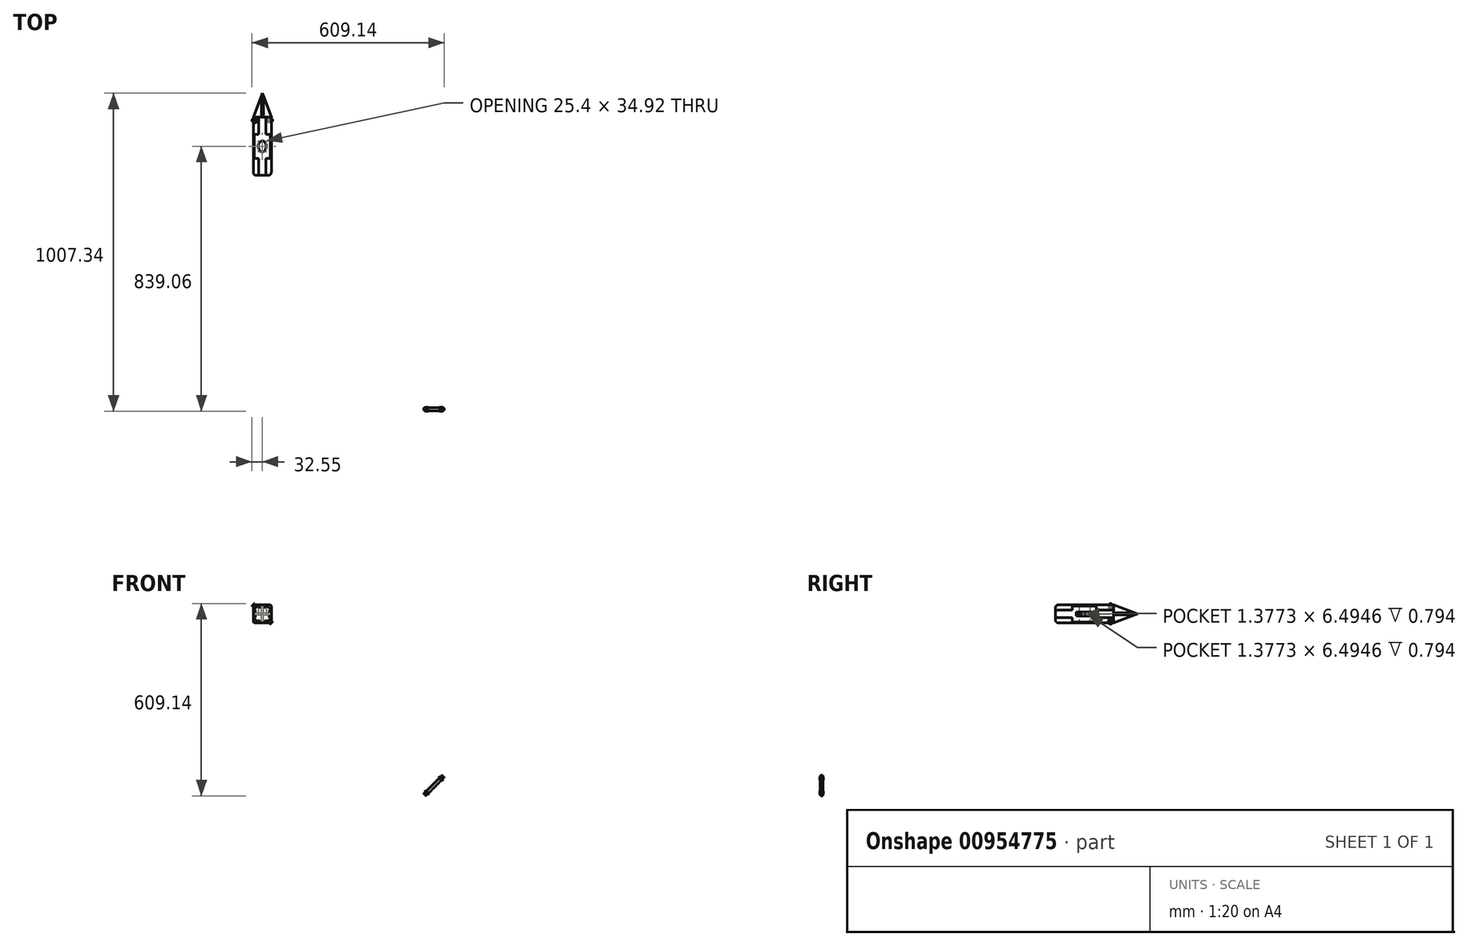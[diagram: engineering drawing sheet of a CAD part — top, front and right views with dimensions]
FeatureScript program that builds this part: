
annotation { "Feature Type Name" : "Feature", "Feature Type Description" : "" }
export const myFeature = defineFeature(function(context is Context, id is Id, definition is map)
    precondition{}
    {
        {
            var Q0;
            Q0=qCreatedBy(makeId("Top.planeOp"),FACE);
            var sketch = newSketch(context, id + "F0", { "sketchPlane" : qUnion([Q0])});
            skEllipse(sketch, "E0", {"center": v(0, 0) * mm, "majorRadius": 12.7 * mm, "minorRadius": 17.46 * mm, "majorAxis": v(1, 0)});
            skSolve(sketch);
        }
        {
            var Q0;
            Q0=qSketchRegion(id+"F0",true);
            extrude(context, id + "F1", {"entities" : qUnion([Q0]), "depth" : 1219.2 * mm, "offsetDistance" : 25.4 * mm});
        }
        {
            var Q0;
            Q0=qCreatedBy(makeId("Front.planeOp"),FACE);
            var sketch = newSketch(context, id + "F2", { "sketchPlane" : qUnion([Q0])});
            skCircle(sketch, "E1.cCircle", {"center": v(0, 1177.87) * mm, "radius": 30.93 * mm, "construction": true});
            skLineSegment(sketch, "E1.0", {"start": v(28.57, 1189.7) * mm, "end": v(28.57, 1166.03) * mm});
            skLineSegment(sketch, "E1.1", {"start": v(28.57, 1166.03) * mm, "end": v(11.84, 1149.3) * mm});
            skLineSegment(sketch, "E1.2", {"start": v(11.84, 1149.3) * mm, "end": v(-11.84, 1149.3) * mm});
            skLineSegment(sketch, "E1.3", {"start": v(-11.84, 1149.3) * mm, "end": v(-28.58, 1166.03) * mm});
            skLineSegment(sketch, "E1.4", {"start": v(-28.58, 1166.03) * mm, "end": v(-28.58, 1189.7) * mm});
            skLineSegment(sketch, "E1.5", {"start": v(-28.57, 1189.7) * mm, "end": v(-11.84, 1206.44) * mm});
            skLineSegment(sketch, "E1.6", {"start": v(-11.84, 1206.44) * mm, "end": v(11.84, 1206.44) * mm});
            skLineSegment(sketch, "E1.7", {"start": v(11.84, 1206.44) * mm, "end": v(28.57, 1189.7) * mm});
            skLineSegment(sketch, "E2.bottom", {"start": v(28.57, 1206.44) * mm, "end": v(-28.58, 1206.44) * mm});
            skLineSegment(sketch, "E2.top", {"start": v(28.57, 1149.3) * mm, "end": v(-28.58, 1149.3) * mm});
            skLineSegment(sketch, "E2.left", {"start": v(28.57, 1206.44) * mm, "end": v(28.57, 1149.3) * mm});
            skLineSegment(sketch, "E2.right", {"start": v(-28.58, 1206.44) * mm, "end": v(-28.58, 1149.3) * mm});
            skSolve(sketch);
        }
        {
            var Q0;
            {var subQ0=sQuery(id+"F2.wireOp",EDGE,"E1.5");Q0=makeQuery(id+"F2.imprint","IMPRINT",FACE,{"disambiguationData":[TD([[makeQuery(id+"F2.imprint","IMPRINT",EDGE,{"derivedFrom":subQ0}),1.0]])]});}
            var Q1;
            {var subQ0=sQuery(id+"F2.wireOp",EDGE,"E1.7");Q1=makeQuery(id+"F2.imprint","IMPRINT",FACE,{"disambiguationData":[TD([[makeQuery(id+"F2.imprint","IMPRINT",EDGE,{"derivedFrom":subQ0}),1.0]])]});}
            var Q2;
            {var subQ4=sQuery(id+"F2.wireOp",EDGE,"E1.1");Q2=makeQuery(id+"F2.imprint","IMPRINT",FACE,{"disambiguationData":[TD([[makeQuery(id+"F2.imprint","IMPRINT",EDGE,{"derivedFrom":subQ4}),-1.0]])]});}
            var Q3;
            {var subQ0=sQuery(id+"F2.wireOp",EDGE,"E1.3");Q3=makeQuery(id+"F2.imprint","IMPRINT",FACE,{"disambiguationData":[TD([[makeQuery(id+"F2.imprint","IMPRINT",EDGE,{"derivedFrom":subQ0}),1.0]])]});}
            var Q4;
            {var subQ0=sQuery(id+"F2.wireOp",EDGE,"E1.1");Q4=makeQuery(id+"F2.imprint","IMPRINT",FACE,{"disambiguationData":[TD([[makeQuery(id+"F2.imprint","IMPRINT",EDGE,{"derivedFrom":subQ0}),1.0]])]});}
            extrude(context, id + "F3", {"entities" : qUnion([Q0, Q1, Q2, Q3, Q4]), "depth" : 38.1 * mm, "offsetDistance" : 25.4 * mm, "hasSecondDirection" : true, "secondDirectionOppositeDirection" : true, "secondDirectionDepth" : 38.1 * mm});
        }
        {
            var Q0;
            {var subQ4=sQuery(id+"F2.wireOp",EDGE,"E1.1");Q0=makeQuery(id+"F2.imprint","IMPRINT",FACE,{"disambiguationData":[TD([[makeQuery(id+"F2.imprint","IMPRINT",EDGE,{"derivedFrom":subQ4}),-1.0]])]});}
            extrude(context, id + "F4", {"entities" : qUnion([Q0]), "operationType" : NewBodyOperationType.ADD, "depth" : 92.07 * mm, "offsetDistance" : 25.4 * mm, "hasSecondDirection" : true, "secondDirectionOppositeDirection" : true, "secondDirectionDepth" : 92.07 * mm});
        }
        {
            var Q0;
            Q0=makeQuery(id+"F4.opExtrude","CAP_FACE",FACE,{"disambiguationData":[OSD([sQuery(id+"F2.wireOp",EDGE,"E1.1"),sQuery(id+"F2.wireOp",EDGE,"E1.3"),sQuery(id+"F2.wireOp",EDGE,"E1.5"),sQuery(id+"F2.wireOp",EDGE,"E1.7"),sQuery(id+"F2.wireOp",EDGE,"E2.bottom"),sQuery(id+"F2.wireOp",EDGE,"E2.top"),sQuery(id+"F2.wireOp",EDGE,"E2.left"),sQuery(id+"F2.wireOp",EDGE,"E2.right")])],"isStart":false});
            fillet(context, id + "F5", {"entities" : qUnion([Q0]), "radius" : 9.52 * mm, "tangentPropagation" : true, "allowEdgeOverflow" : false});
        }
        {
            var Q0;
            Q0=makeQuery(id+"F3.opExtrude","SWEPT_EDGE",EDGE,{"disambiguationData":[OSD([sQuery(id+"F2.wireOp",EDGE,"E2.bottom"),sQuery(id+"F2.wireOp",EDGE,"E2.left")])]});
            var Q1;
            Q1=makeQuery(id+"F3.opExtrude","SWEPT_EDGE",EDGE,{"disambiguationData":[OSD([sQuery(id+"F2.wireOp",EDGE,"E2.top"),sQuery(id+"F2.wireOp",EDGE,"E2.left")])]});
            var Q2;
            Q2=makeQuery(id+"F3.opExtrude","SWEPT_EDGE",EDGE,{"disambiguationData":[OSD([sQuery(id+"F2.wireOp",EDGE,"E2.bottom"),sQuery(id+"F2.wireOp",EDGE,"E2.right")])]});
            var Q3;
            Q3=makeQuery(id+"F3.opExtrude","SWEPT_EDGE",EDGE,{"disambiguationData":[OSD([sQuery(id+"F2.wireOp",EDGE,"E2.top"),sQuery(id+"F2.wireOp",EDGE,"E2.right")])]});
            chamfer(context, id + "F6", {"entities" : qUnion([Q0, Q1, Q2, Q3]), "width" : 3.17 * mm, "tangentPropagation" : true});
        }
        {
            var Q0;
            Q0=qSketchRegion(id+"F0",true);
            extrude(context, id + "F7", {"entities" : qUnion([Q0]), "operationType" : NewBodyOperationType.REMOVE, "depth" : 1219.2 * mm, "offsetDistance" : 25.4 * mm});
        }
        {
            var Q0;
            {var subQ0=sQuery(id+"F2.wireOp",EDGE,"E2.left");Q0=makeQuery(id+"F4.boolean.opBoolean","MERGE",FACE,{"derivedFrom":[makeQuery(id+"F3.opExtrude","SWEPT_FACE",FACE,{"disambiguationData":[OSD([subQ0])]}),makeQuery(id+"F4.opExtrude","SWEPT_FACE",FACE,{"disambiguationData":[OSD([subQ0])]})]});}
            var sketch = newSketch(context, id + "F8", { "sketchPlane" : qUnion([Q0])});
            skLineSegment(sketch, "E3.bottom", {"start": v(28.57, 1162) * mm, "end": v(-28.58, 1162) * mm, "construction": true});
            skLineSegment(sketch, "E3.top", {"start": v(28.57, 1193.74) * mm, "end": v(-28.58, 1193.74) * mm, "construction": true});
            skLineSegment(sketch, "E3.left", {"start": v(28.57, 1162) * mm, "end": v(28.57, 1193.74) * mm, "construction": true});
            skLineSegment(sketch, "E3.right", {"start": v(-28.57, 1162) * mm, "end": v(-28.57, 1193.74) * mm, "construction": true});
            skPoint(sketch, "E3.middle", {"position": v(0, 1177.87) * mm});
            skLineSegment(sketch, "E4", {"start": v(0, 1193.74) * mm, "end": v(-28.58, 1177.87) * mm, "construction": true});
            skLineSegment(sketch, "E5", {"start": v(-28.57, 1177.87) * mm, "end": v(0, 1162) * mm, "construction": true});
            skLineSegment(sketch, "E6", {"start": v(0, 1162) * mm, "end": v(28.58, 1177.87) * mm, "construction": true});
            skLineSegment(sketch, "E7", {"start": v(28.58, 1177.87) * mm, "end": v(0, 1193.74) * mm, "construction": true});
            skLineSegment(sketch, "E8.bottom", {"start": v(24.29, 1173.01) * mm, "end": v(-24.29, 1173.01) * mm});
            skLineSegment(sketch, "E8.top", {"start": v(24.29, 1182.72) * mm, "end": v(-24.29, 1182.72) * mm});
            skLineSegment(sketch, "E8.left", {"start": v(24.29, 1173.01) * mm, "end": v(24.29, 1182.72) * mm});
            skLineSegment(sketch, "E8.right", {"start": v(-24.29, 1173.01) * mm, "end": v(-24.29, 1182.72) * mm});
            skLineSegment(sketch, "E9.bottom", {"start": v(25.87, 1171.43) * mm, "end": v(-25.87, 1171.43) * mm});
            skLineSegment(sketch, "E9.top", {"start": v(25.87, 1184.3) * mm, "end": v(-25.87, 1184.3) * mm});
            skLineSegment(sketch, "E9.left", {"start": v(25.87, 1171.43) * mm, "end": v(25.87, 1184.3) * mm});
            skLineSegment(sketch, "E9.right", {"start": v(-25.87, 1171.43) * mm, "end": v(-25.87, 1184.3) * mm});
            skPoint(sketch, "E10.sketch_text.left.end.orphan", {"position": v(-22.7, 1181.13) * mm});
            skPoint(sketch, "E11", {"position": v(22.7, 1181.13) * mm});
            skPoint(sketch, "E12", {"position": v(22.7, 1174.6) * mm});
            skPoint(sketch, "E13", {"position": v(-22.7, 1174.6) * mm});
            skText(sketch, "E14", { "text": "ARTILLIER", "fontName": "OpenSans-Bold.ttf"});
            const initialGuessF8  = {"E14": [-0.02283, 1.1746, 1, 0, 0.00655]};
            skSetInitialGuess(sketch, initialGuessF8);
            skSolve(sketch);
        }
        {
            var Q0;
            Q0=makeQuery(id+"F8.imprint","IMPRINT",FACE,{"disambiguationData":[TD([[makeQuery(id+"F8.imprint","IMPRINT",EDGE,{"derivedFrom":sQuery(id+"F8.wireOp",EDGE,"E14.sketch_text.stroke-0")}),-1.0]])]});
            var Q1;
            Q1=makeQuery(id+"F8.imprint","IMPRINT",FACE,{"disambiguationData":[TD([[makeQuery(id+"F8.imprint","IMPRINT",EDGE,{"derivedFrom":sQuery(id+"F8.wireOp",EDGE,"E14.sketch_text.stroke-12")}),-1.0]])]});
            var Q2;
            Q2=makeQuery(id+"F8.imprint","IMPRINT",FACE,{"disambiguationData":[TD([[makeQuery(id+"F8.imprint","IMPRINT",EDGE,{"derivedFrom":sQuery(id+"F8.wireOp",EDGE,"E14.sketch_text.stroke-31")}),-1.0]])]});
            var Q3;
            Q3=makeQuery(id+"F8.imprint","IMPRINT",FACE,{"disambiguationData":[TD([[makeQuery(id+"F8.imprint","IMPRINT",EDGE,{"derivedFrom":sQuery(id+"F8.wireOp",EDGE,"E14.sketch_text.stroke-39")}),-1.0]])]});
            var Q4;
            Q4=makeQuery(id+"F8.imprint","IMPRINT",FACE,{"disambiguationData":[TD([[makeQuery(id+"F8.imprint","IMPRINT",EDGE,{"derivedFrom":sQuery(id+"F8.wireOp",EDGE,"E14.sketch_text.stroke-43")}),-1.0]])]});
            var Q5;
            Q5=makeQuery(id+"F8.imprint","IMPRINT",FACE,{"disambiguationData":[TD([[makeQuery(id+"F8.imprint","IMPRINT",EDGE,{"derivedFrom":sQuery(id+"F8.wireOp",EDGE,"E8.bottom")}),1.0]])]});
            var Q6;
            Q6=makeQuery(id+"F8.imprint","IMPRINT",FACE,{"disambiguationData":[TD([[makeQuery(id+"F8.imprint","IMPRINT",EDGE,{"derivedFrom":sQuery(id+"F8.wireOp",EDGE,"E14.sketch_text.stroke-49")}),-1.0]])]});
            var Q7;
            Q7=makeQuery(id+"F8.imprint","IMPRINT",FACE,{"disambiguationData":[TD([[makeQuery(id+"F8.imprint","IMPRINT",EDGE,{"derivedFrom":sQuery(id+"F8.wireOp",EDGE,"E14.sketch_text.stroke-55")}),-1.0]])]});
            var Q8;
            Q8=makeQuery(id+"F8.imprint","IMPRINT",FACE,{"disambiguationData":[TD([[makeQuery(id+"F8.imprint","IMPRINT",EDGE,{"derivedFrom":sQuery(id+"F8.wireOp",EDGE,"E14.sketch_text.stroke-59")}),-1.0]])]});
            var Q9;
            Q9=makeQuery(id+"F8.imprint","IMPRINT",FACE,{"disambiguationData":[TD([[makeQuery(id+"F8.imprint","IMPRINT",EDGE,{"derivedFrom":sQuery(id+"F8.wireOp",EDGE,"E14.sketch_text.stroke-71")}),-1.0]])]});
            extrude(context, id + "F9", {"entities" : qUnion([Q0, Q1, Q2, Q3, Q4, Q5, Q6, Q7, Q8, Q9]), "operationType" : NewBodyOperationType.REMOVE, "oppositeDirection" : true, "depth" : 0.8 * mm, "offsetDistance" : 25.4 * mm});
        }
        {
            var Q0;
            {var subQ0=sQuery(id+"F2.wireOp",EDGE,"E2.right");Q0=makeQuery(id+"F4.boolean.opBoolean","MERGE",FACE,{"derivedFrom":[makeQuery(id+"F3.opExtrude","SWEPT_FACE",FACE,{"disambiguationData":[OSD([subQ0])]}),makeQuery(id+"F4.opExtrude","SWEPT_FACE",FACE,{"disambiguationData":[OSD([subQ0])]})]});}
            var sketch = newSketch(context, id + "F10", { "sketchPlane" : qUnion([Q0])});
            skLineSegment(sketch, "E15.bottom", {"start": v(28.57, 1162.05) * mm, "end": v(-28.57, 1162.05) * mm, "construction": true});
            skLineSegment(sketch, "E15.top", {"start": v(28.57, 1193.8) * mm, "end": v(-28.57, 1193.8) * mm, "construction": true});
            skLineSegment(sketch, "E15.left", {"start": v(28.57, 1162.05) * mm, "end": v(28.57, 1193.8) * mm, "construction": true});
            skLineSegment(sketch, "E15.right", {"start": v(-28.57, 1162.05) * mm, "end": v(-28.57, 1193.8) * mm, "construction": true});
            skPoint(sketch, "E15.middle", {"position": v(0, 1177.93) * mm});
            skLineSegment(sketch, "E16", {"start": v(0, 1193.8) * mm, "end": v(-28.57, 1177.93) * mm, "construction": true});
            skLineSegment(sketch, "E17", {"start": v(-28.57, 1177.93) * mm, "end": v(0, 1162.05) * mm, "construction": true});
            skLineSegment(sketch, "E18", {"start": v(0, 1162.05) * mm, "end": v(28.57, 1177.93) * mm, "construction": true});
            skLineSegment(sketch, "E19", {"start": v(28.57, 1177.93) * mm, "end": v(0, 1193.8) * mm, "construction": true});
            skLineSegment(sketch, "E20.bottom", {"start": v(24.29, 1173.07) * mm, "end": v(-24.29, 1173.07) * mm});
            skLineSegment(sketch, "E20.top", {"start": v(24.29, 1182.78) * mm, "end": v(-24.29, 1182.78) * mm});
            skLineSegment(sketch, "E20.left", {"start": v(24.29, 1173.07) * mm, "end": v(24.29, 1182.78) * mm});
            skLineSegment(sketch, "E20.right", {"start": v(-24.29, 1173.07) * mm, "end": v(-24.29, 1182.78) * mm});
            skLineSegment(sketch, "E21.bottom", {"start": v(25.87, 1171.49) * mm, "end": v(-25.87, 1171.49) * mm});
            skLineSegment(sketch, "E21.top", {"start": v(25.87, 1184.36) * mm, "end": v(-25.87, 1184.36) * mm});
            skLineSegment(sketch, "E21.left", {"start": v(25.87, 1171.49) * mm, "end": v(25.87, 1184.36) * mm});
            skLineSegment(sketch, "E21.right", {"start": v(-25.87, 1171.49) * mm, "end": v(-25.87, 1184.36) * mm});
            skPoint(sketch, "E22.sketch_text.left.end.orphan", {"position": v(-22.7, 1181.19) * mm});
            skText(sketch, "E23", { "text": "ARTILLIER", "fontName": "OpenSans-Bold.ttf"});
            const initialGuessF10  = {"E23": [-0.02243, 1.17481, 1, 0, 0.00653]};
            skSetInitialGuess(sketch, initialGuessF10);
            skSolve(sketch);
        }
        {
            var Q0;
            Q0=makeQuery(id+"F10.imprint","IMPRINT",FACE,{"disambiguationData":[TD([[makeQuery(id+"F10.imprint","IMPRINT",EDGE,{"derivedFrom":sQuery(id+"F10.wireOp",EDGE,"E20.bottom")}),1.0]])]});
            var Q1;
            Q1=makeQuery(id+"F10.imprint","IMPRINT",FACE,{"disambiguationData":[TD([[makeQuery(id+"F10.imprint","IMPRINT",EDGE,{"derivedFrom":sQuery(id+"F10.wireOp",EDGE,"E23.sketch_text.stroke-0")}),-1.0]])]});
            var Q2;
            Q2=makeQuery(id+"F10.imprint","IMPRINT",FACE,{"disambiguationData":[TD([[makeQuery(id+"F10.imprint","IMPRINT",EDGE,{"derivedFrom":sQuery(id+"F10.wireOp",EDGE,"E23.sketch_text.stroke-12")}),-1.0]])]});
            var Q3;
            Q3=makeQuery(id+"F10.imprint","IMPRINT",FACE,{"disambiguationData":[TD([[makeQuery(id+"F10.imprint","IMPRINT",EDGE,{"derivedFrom":sQuery(id+"F10.wireOp",EDGE,"E23.sketch_text.stroke-39")}),-1.0]])]});
            var Q4;
            Q4=makeQuery(id+"F10.imprint","IMPRINT",FACE,{"disambiguationData":[TD([[makeQuery(id+"F10.imprint","IMPRINT",EDGE,{"derivedFrom":sQuery(id+"F10.wireOp",EDGE,"E23.sketch_text.stroke-43")}),-1.0]])]});
            var Q5;
            Q5=makeQuery(id+"F10.imprint","IMPRINT",FACE,{"disambiguationData":[TD([[makeQuery(id+"F10.imprint","IMPRINT",EDGE,{"derivedFrom":sQuery(id+"F10.wireOp",EDGE,"E23.sketch_text.stroke-31")}),-1.0]])]});
            var Q6;
            Q6=makeQuery(id+"F10.imprint","IMPRINT",FACE,{"disambiguationData":[TD([[makeQuery(id+"F10.imprint","IMPRINT",EDGE,{"derivedFrom":sQuery(id+"F10.wireOp",EDGE,"E23.sketch_text.stroke-55")}),-1.0]])]});
            var Q7;
            Q7=makeQuery(id+"F10.imprint","IMPRINT",FACE,{"disambiguationData":[TD([[makeQuery(id+"F10.imprint","IMPRINT",EDGE,{"derivedFrom":sQuery(id+"F10.wireOp",EDGE,"E23.sketch_text.stroke-59")}),-1.0]])]});
            var Q8;
            Q8=makeQuery(id+"F10.imprint","IMPRINT",FACE,{"disambiguationData":[TD([[makeQuery(id+"F10.imprint","IMPRINT",EDGE,{"derivedFrom":sQuery(id+"F10.wireOp",EDGE,"E23.sketch_text.stroke-71")}),-1.0]])]});
            var Q9;
            Q9=makeQuery(id+"F10.imprint","IMPRINT",FACE,{"disambiguationData":[TD([[makeQuery(id+"F10.imprint","IMPRINT",EDGE,{"derivedFrom":sQuery(id+"F10.wireOp",EDGE,"E23.sketch_text.stroke-49")}),-1.0]])]});
            extrude(context, id + "F11", {"entities" : qUnion([Q0, Q1, Q2, Q3, Q4, Q5, Q6, Q7, Q8, Q9]), "operationType" : NewBodyOperationType.REMOVE, "oppositeDirection" : true, "depth" : 0.8 * mm, "offsetDistance" : 25.4 * mm});
        }
        {
            var Q0;
            Q0=makeQuery(id+"F4.opExtrude","CAP_FACE",FACE,{"disambiguationData":[OSD([sQuery(id+"F2.wireOp",EDGE,"E1.1"),sQuery(id+"F2.wireOp",EDGE,"E1.3"),sQuery(id+"F2.wireOp",EDGE,"E1.5"),sQuery(id+"F2.wireOp",EDGE,"E1.7"),sQuery(id+"F2.wireOp",EDGE,"E2.bottom"),sQuery(id+"F2.wireOp",EDGE,"E2.top"),sQuery(id+"F2.wireOp",EDGE,"E2.left"),sQuery(id+"F2.wireOp",EDGE,"E2.right")])],"isStart":true});
            var sketch = newSketch(context, id + "F12", { "sketchPlane" : qUnion([Q0])});
            skLineSegment(sketch, "E24.bottom", {"start": v(3.18, 1149.3) * mm, "end": v(-3.17, 1149.3) * mm});
            skLineSegment(sketch, "E24.top", {"start": v(3.18, 1206.44) * mm, "end": v(-3.17, 1206.44) * mm});
            skLineSegment(sketch, "E24.left", {"start": v(3.18, 1149.3) * mm, "end": v(3.18, 1174.7) * mm});
            skLineSegment(sketch, "E24.right", {"start": v(-3.17, 1149.3) * mm, "end": v(-3.17, 1174.7) * mm});
            skPoint(sketch, "E24.middle", {"position": v(0, 1177.87) * mm});
            skLineSegment(sketch, "E25.bottom", {"start": v(28.58, 1174.7) * mm, "end": v(3.18, 1174.7) * mm});
            skLineSegment(sketch, "E25.top", {"start": v(28.58, 1181.04) * mm, "end": v(3.18, 1181.04) * mm});
            skLineSegment(sketch, "E25.left", {"start": v(28.58, 1174.7) * mm, "end": v(28.58, 1181.04) * mm});
            skLineSegment(sketch, "E25.right", {"start": v(-28.58, 1174.7) * mm, "end": v(-28.58, 1181.04) * mm});
            skLineSegment(sketch, "E26.trimOffspring", {"start": v(-3.17, 1181.04) * mm, "end": v(-28.58, 1181.04) * mm});
            skLineSegment(sketch, "E27.trimOffspring", {"start": v(-3.17, 1181.04) * mm, "end": v(-3.17, 1206.44) * mm});
            skLineSegment(sketch, "E28.trimOffspring", {"start": v(-3.17, 1174.7) * mm, "end": v(-28.58, 1174.7) * mm});
            skLineSegment(sketch, "E29.trimOffspring", {"start": v(3.18, 1181.04) * mm, "end": v(3.18, 1206.44) * mm});
            skSolve(sketch);
        }
        {
            var Q0;
            Q0=makeQuery(id+"F12.imprint","IMPRINT",FACE,{"disambiguationData":[TD([[makeQuery(id+"F12.imprint","IMPRINT",EDGE,{"derivedFrom":sQuery(id+"F12.wireOp",EDGE,"E24.bottom")}),1.0]])]});
            extrude(context, id + "F13", {"entities" : qUnion([Q0]), "operationType" : NewBodyOperationType.REMOVE, "oppositeDirection" : true, "depth" : 38.1 * mm, "offsetDistance" : 25.4 * mm});
        }
        {
            var Q0;
            Q0=makeQuery(id+"F12.imprint","IMPRINT",FACE,{"disambiguationData":[TD([[makeQuery(id+"F12.imprint","IMPRINT",EDGE,{"derivedFrom":sQuery(id+"F12.wireOp",EDGE,"E24.bottom")}),1.0]])]});
            extrude(context, id + "F14", {"entities" : qUnion([Q0]), "oppositeDirection" : true, "depth" : 38.1 * mm, "offsetDistance" : 25.4 * mm});
        }
        {
            var Q0;
            Q0=makeQuery(id+"F14.opExtrude","CAP_FACE",FACE,{"disambiguationData":[OSD([sQuery(id+"F12.wireOp",EDGE,"E24.bottom"),sQuery(id+"F12.wireOp",EDGE,"E24.top"),sQuery(id+"F12.wireOp",EDGE,"E24.left"),sQuery(id+"F12.wireOp",EDGE,"E24.right"),sQuery(id+"F12.wireOp",EDGE,"E25.bottom"),sQuery(id+"F12.wireOp",EDGE,"E25.top"),sQuery(id+"F12.wireOp",EDGE,"E25.left"),sQuery(id+"F12.wireOp",EDGE,"E25.right"),sQuery(id+"F12.wireOp",EDGE,"E26.trimOffspring"),sQuery(id+"F12.wireOp",EDGE,"E27.trimOffspring"),sQuery(id+"F12.wireOp",EDGE,"E28.trimOffspring"),sQuery(id+"F12.wireOp",EDGE,"E29.trimOffspring")])],"isStart":true});
            extrude(context, id + "F15", {"entities" : qUnion([Q0]), "operationType" : NewBodyOperationType.ADD, "depth" : 76.2 * mm, "offsetDistance" : 25.4 * mm});
        }
        {
            var Q0;
            {var subQ0=sQuery(id+"F12.wireOp",EDGE,"E27.trimOffspring");Q0=makeQuery(id+"F15.boolean.opBoolean","MERGE",FACE,{"derivedFrom":[makeQuery(id+"F14.opExtrude","SWEPT_FACE",FACE,{"disambiguationData":[OSD([subQ0])]}),makeQuery(id+"F15.opExtrude","SWEPT_FACE",FACE,{"disambiguationData":[OSD([subQ0])]})]});}
            var sketch = newSketch(context, id + "F16", { "sketchPlane" : qUnion([Q0])});
            skLineSegment(sketch, "E30.bottom", {"start": v(168.28, 1206.44) * mm, "end": v(92.07, 1206.44) * mm});
            skLineSegment(sketch, "E30.top", {"start": v(168.28, 1149.3) * mm, "end": v(92.07, 1149.3) * mm});
            skLineSegment(sketch, "E30.left", {"start": v(168.28, 1206.44) * mm, "end": v(168.28, 1149.3) * mm});
            skLineSegment(sketch, "E30.right", {"start": v(92.07, 1206.44) * mm, "end": v(92.07, 1149.3) * mm, "construction": true});
            skLineSegment(sketch, "E31", {"start": v(92.08, 1206.44) * mm, "end": v(168.28, 1177.87) * mm});
            skLineSegment(sketch, "E32", {"start": v(168.28, 1177.87) * mm, "end": v(92.08, 1149.3) * mm});
            skSolve(sketch);
        }
        {
            var Q0;
            {var subQ0=sQuery(id+"F16.wireOp",EDGE,"E30.left");var subQ5=sQuery(id+"F16.wireOp",EDGE,"E31");var subQ6=makeQuery(id+"F16.imprint","INTERSECT",VERTEX,{"derivedFrom":[subQ0,subQ5,sQuery(id+"F16.wireOp",EDGE,"E32")]});Q0=makeQuery(id+"F16.imprint","IMPRINT",FACE,{"disambiguationData":[TD([[makeQuery(id+"F16.imprint","IMPRINT",EDGE,{"disambiguationData":[TD([[subQ6,1.0]])],"derivedFrom":subQ0}),-1.0]])]});}
            var Q1;
            {var subQ0=sQuery(id+"F16.wireOp",EDGE,"E30.top");Q1=makeQuery(id+"F16.imprint","IMPRINT",FACE,{"disambiguationData":[TD([[makeQuery(id+"F16.imprint","IMPRINT",EDGE,{"derivedFrom":subQ0}),-1.0]])]});}
            var Q2;
            {var subQ0=sQuery(id+"F16.wireOp",EDGE,"E30.bottom");Q2=makeQuery(id+"F16.imprint","IMPRINT",FACE,{"disambiguationData":[TD([[makeQuery(id+"F16.imprint","IMPRINT",EDGE,{"derivedFrom":subQ0}),-1.0]])]});}
            extrude(context, id + "F17", {"entities" : qUnion([Q0, Q1, Q2]), "operationType" : NewBodyOperationType.REMOVE, "oppositeDirection" : true, "depth" : 31.75 * mm, "offsetDistance" : 25.4 * mm, "hasSecondDirection" : true, "secondDirectionOppositeDirection" : false, "secondDirectionDepth" : 25.4 * mm});
        }
        {
            var Q0;
            {var subQ0=sQuery(id+"F12.wireOp",EDGE,"E26.trimOffspring");Q0=makeQuery(id+"F15.boolean.opBoolean","MERGE",FACE,{"derivedFrom":[makeQuery(id+"F14.opExtrude","SWEPT_FACE",FACE,{"disambiguationData":[OSD([subQ0])]}),makeQuery(id+"F15.opExtrude","SWEPT_FACE",FACE,{"disambiguationData":[OSD([subQ0])]})]});}
            var sketch = newSketch(context, id + "F18", { "sketchPlane" : qUnion([Q0])});
            skLineSegment(sketch, "E33.bottom", {"start": v(28.57, 168.28) * mm, "end": v(-28.58, 168.28) * mm});
            skLineSegment(sketch, "E33.top", {"start": v(28.57, 92.08) * mm, "end": v(-28.58, 92.08) * mm, "construction": true});
            skLineSegment(sketch, "E33.left", {"start": v(28.57, 168.28) * mm, "end": v(28.57, 92.08) * mm});
            skLineSegment(sketch, "E33.right", {"start": v(-28.58, 168.28) * mm, "end": v(-28.58, 92.07) * mm});
            skLineSegment(sketch, "E34", {"start": v(-28.58, 92.08) * mm, "end": v(0, 168.28) * mm});
            skLineSegment(sketch, "E35", {"start": v(0, 168.28) * mm, "end": v(28.57, 92.08) * mm});
            skSolve(sketch);
        }
        {
            var Q0;
            {var subQ5=sQuery(id+"F12.wireOp",EDGE,"E26.trimOffspring");var subQ6=makeQuery(id+"F17.boolean.opBoolean","INTERSECT",EDGE,{"derivedFrom":[makeQuery(id+"F15.boolean.opBoolean","MERGE",FACE,{"derivedFrom":[makeQuery(id+"F14.opExtrude","SWEPT_FACE",FACE,{"disambiguationData":[OSD([subQ5])]}),makeQuery(id+"F15.opExtrude","SWEPT_FACE",FACE,{"disambiguationData":[OSD([subQ5])]})]}),makeQuery(id+"F17.opExtrude","SWEPT_FACE",FACE,{"disambiguationData":[OSD([sQuery(id+"F16.wireOp",EDGE,"E31")])]})]});Q0=makeQuery(id+"F18.imprint","IMPRINT",FACE,{"disambiguationData":[TD([[makeQuery(id+"F18.imprint","IMPRINT",EDGE,{"derivedFrom":subQ6}),1.0]])]});}
            var Q1;
            {var subQ0=sQuery(id+"F18.wireOp",EDGE,"E33.right");Q1=makeQuery(id+"F18.imprint","IMPRINT",FACE,{"disambiguationData":[TD([[makeQuery(id+"F18.imprint","IMPRINT",EDGE,{"derivedFrom":subQ0}),1.0]])]});}
            var Q2;
            {var subQ1=sQuery(id+"F12.wireOp",EDGE,"E26.trimOffspring");var subQ2=makeQuery(id+"F17.boolean.opBoolean","INTERSECT",EDGE,{"derivedFrom":[makeQuery(id+"F15.boolean.opBoolean","MERGE",FACE,{"derivedFrom":[makeQuery(id+"F14.opExtrude","SWEPT_FACE",FACE,{"disambiguationData":[OSD([subQ1])]}),makeQuery(id+"F15.opExtrude","SWEPT_FACE",FACE,{"disambiguationData":[OSD([subQ1])]})]}),makeQuery(id+"F17.opExtrude","SWEPT_FACE",FACE,{"disambiguationData":[OSD([sQuery(id+"F16.wireOp",EDGE,"E31")])]})]});Q2=makeQuery(id+"F18.imprint","IMPRINT",FACE,{"disambiguationData":[TD([[makeQuery(id+"F18.imprint","IMPRINT",EDGE,{"derivedFrom":subQ2}),-1.0]])]});}
            extrude(context, id + "F19", {"entities" : qUnion([Q0, Q1, Q2]), "operationType" : NewBodyOperationType.REMOVE, "oppositeDirection" : true, "depth" : 25.4 * mm, "offsetDistance" : 25.4 * mm});
        }
        {
            var Q0;
            {var subQ0=sQuery(id+"F2.wireOp",EDGE,"E2.right");var subQ1=sQuery(id+"F2.wireOp",EDGE,"E2.left");var subQ2=sQuery(id+"F2.wireOp",EDGE,"E2.top");var subQ3=sQuery(id+"F2.wireOp",EDGE,"E2.bottom");var subQ4=sQuery(id+"F2.wireOp",EDGE,"E1.5");Q0=makeQuery(id+"F4.boolean.opBoolean","SPLIT",FACE,{"disambiguationData":[TD([makeQuery(id+"F3.opExtrude","CAP_FACE",FACE,{"disambiguationData":[OSD([subQ3,subQ2,subQ1,subQ0])],"isStart":true})])],"derivedFrom":makeQuery(id+"F4.opExtrude","SWEPT_FACE",FACE,{"disambiguationData":[OSD([subQ4])]})});}
            var sketch = newSketch(context, id + "F20", { "sketchPlane" : qUnion([Q0])});
            skLineSegment(sketch, "E36.bottom", {"start": v(-92.08, 844.71) * mm, "end": v(-38.1, 844.71) * mm, "construction": true});
            skLineSegment(sketch, "E36.top", {"start": v(-92.08, 821.04) * mm, "end": v(-38.1, 821.04) * mm, "construction": true});
            skLineSegment(sketch, "E36.left", {"start": v(-92.08, 844.71) * mm, "end": v(-92.08, 821.04) * mm, "construction": true});
            skLineSegment(sketch, "E36.right", {"start": v(-38.1, 844.71) * mm, "end": v(-38.1, 821.04) * mm, "construction": true});
            skLineSegment(sketch, "E37", {"start": v(-92.08, 832.88) * mm, "end": v(-65.09, 832.88) * mm, "construction": true});
            skPoint(sketch, "E37.endSnap0", {"position": v(-65.09, 844.71) * mm});
            skCircle(sketch, "E38", {"center": v(-82.55, 832.88) * mm, "radius": 4.76 * mm});
            skCircle(sketch, "E39.cCircle", {"center": v(-82.55, 832.88) * mm, "radius": 6.19 * mm, "construction": true});
            skLineSegment(sketch, "E39.0", {"start": v(-78.98, 826.7) * mm, "end": v(-86.12, 826.7) * mm});
            skLineSegment(sketch, "E39.1", {"start": v(-86.12, 826.7) * mm, "end": v(-89.7, 832.88) * mm});
            skLineSegment(sketch, "E39.2", {"start": v(-89.7, 832.88) * mm, "end": v(-86.12, 839.06) * mm});
            skLineSegment(sketch, "E39.3", {"start": v(-86.12, 839.06) * mm, "end": v(-78.98, 839.06) * mm});
            skLineSegment(sketch, "E39.4", {"start": v(-78.98, 839.06) * mm, "end": v(-75.4, 832.88) * mm});
            skLineSegment(sketch, "E39.5", {"start": v(-75.4, 832.88) * mm, "end": v(-78.98, 826.7) * mm});
            skPoint(sketch, "E39.0.midPoint", {"position": v(-82.55, 826.7) * mm});
            skSolve(sketch);
        }
        {
            var Q0;
            Q0=makeQuery(id+"F20.imprint","IMPRINT",FACE,{"disambiguationData":[TD([[makeQuery(id+"F20.imprint","IMPRINT",EDGE,{"derivedFrom":sQuery(id+"F20.wireOp",EDGE,"E38")}),1.0]])]});
            extrude(context, id + "F21", {"entities" : qUnion([Q0]), "operationType" : NewBodyOperationType.ADD, "depth" : 12.7 * mm, "offsetDistance" : 25.4 * mm, "hasSecondDirection" : true, "secondDirectionOppositeDirection" : true, "secondDirectionDepth" : 69.85 * mm});
        }
        {
            var Q0;
            Q0=makeQuery(id+"F20.imprint","IMPRINT",FACE,{"disambiguationData":[TD([[makeQuery(id+"F20.imprint","IMPRINT",EDGE,{"derivedFrom":sQuery(id+"F20.wireOp",EDGE,"E38")}),-1.0]])]});
            extrude(context, id + "F22", {"entities" : qUnion([Q0]), "operationType" : NewBodyOperationType.ADD, "depth" : 6.35 * mm, "offsetDistance" : 25.4 * mm});
        }
        {
            var Q0;
            {var subQ0=sQuery(id+"F2.wireOp",EDGE,"E2.right");var subQ1=sQuery(id+"F2.wireOp",EDGE,"E2.left");var subQ2=sQuery(id+"F2.wireOp",EDGE,"E2.top");var subQ3=sQuery(id+"F2.wireOp",EDGE,"E2.bottom");var subQ4=sQuery(id+"F2.wireOp",EDGE,"E1.7");Q0=makeQuery(id+"F4.boolean.opBoolean","SPLIT",FACE,{"disambiguationData":[TD([makeQuery(id+"F3.opExtrude","CAP_FACE",FACE,{"disambiguationData":[OSD([subQ3,subQ2,subQ1,subQ0])],"isStart":true})])],"derivedFrom":makeQuery(id+"F4.opExtrude","SWEPT_FACE",FACE,{"disambiguationData":[OSD([subQ4])]})});}
            var sketch = newSketch(context, id + "F23", { "sketchPlane" : qUnion([Q0])});
            skLineSegment(sketch, "E40.bottom", {"start": v(-821.04, 38.1) * mm, "end": v(-844.71, 38.1) * mm, "construction": true});
            skLineSegment(sketch, "E40.top", {"start": v(-821.04, 92.08) * mm, "end": v(-844.71, 92.08) * mm, "construction": true});
            skLineSegment(sketch, "E40.left", {"start": v(-821.04, 38.1) * mm, "end": v(-821.04, 92.08) * mm, "construction": true});
            skLineSegment(sketch, "E40.right", {"start": v(-844.71, 38.1) * mm, "end": v(-844.71, 92.08) * mm, "construction": true});
            skLineSegment(sketch, "E41", {"start": v(-832.88, 92.08) * mm, "end": v(-832.88, 53.98) * mm, "construction": true});
            skCircle(sketch, "E42", {"center": v(-832.88, 63.5) * mm, "radius": 4.76 * mm});
            skCircle(sketch, "E43.cCircle", {"center": v(-832.88, 63.5) * mm, "radius": 6.19 * mm, "construction": true});
            skLineSegment(sketch, "E43.0", {"start": v(-826.7, 67.07) * mm, "end": v(-826.7, 59.93) * mm});
            skLineSegment(sketch, "E43.1", {"start": v(-826.7, 59.93) * mm, "end": v(-832.88, 56.36) * mm});
            skLineSegment(sketch, "E43.2", {"start": v(-832.88, 56.36) * mm, "end": v(-839.06, 59.93) * mm});
            skLineSegment(sketch, "E43.3", {"start": v(-839.06, 59.93) * mm, "end": v(-839.06, 67.07) * mm});
            skLineSegment(sketch, "E43.4", {"start": v(-839.06, 67.07) * mm, "end": v(-832.88, 70.64) * mm});
            skLineSegment(sketch, "E43.5", {"start": v(-832.88, 70.64) * mm, "end": v(-826.7, 67.07) * mm});
            skPoint(sketch, "E43.0.midPoint", {"position": v(-826.7, 63.5) * mm});
            skSolve(sketch);
        }
        {
            var Q0;
            Q0=makeQuery(id+"F23.imprint","IMPRINT",FACE,{"disambiguationData":[TD([[makeQuery(id+"F23.imprint","IMPRINT",EDGE,{"derivedFrom":sQuery(id+"F23.wireOp",EDGE,"E42")}),1.0]])]});
            extrude(context, id + "F24", {"entities" : qUnion([Q0]), "operationType" : NewBodyOperationType.ADD, "depth" : 12.7 * mm, "offsetDistance" : 25.4 * mm, "hasSecondDirection" : true, "secondDirectionOppositeDirection" : true, "secondDirectionDepth" : 69.85 * mm});
        }
        {
            var Q0;
            Q0=makeQuery(id+"F23.imprint","IMPRINT",FACE,{"disambiguationData":[TD([[makeQuery(id+"F23.imprint","IMPRINT",EDGE,{"derivedFrom":sQuery(id+"F23.wireOp",EDGE,"E42")}),-1.0]])]});
            extrude(context, id + "F25", {"entities" : qUnion([Q0]), "operationType" : NewBodyOperationType.ADD, "depth" : 6.35 * mm, "offsetDistance" : 25.4 * mm});
        }
        {
            var Q0;
            Q0=makeQuery(id+"F22.opExtrude","CAP_FACE",FACE,{"disambiguationData":[OSD([sQuery(id+"F20.wireOp",EDGE,"E38"),sQuery(id+"F20.wireOp",EDGE,"E39.0"),sQuery(id+"F20.wireOp",EDGE,"E39.1"),sQuery(id+"F20.wireOp",EDGE,"E39.2"),sQuery(id+"F20.wireOp",EDGE,"E39.3"),sQuery(id+"F20.wireOp",EDGE,"E39.4"),sQuery(id+"F20.wireOp",EDGE,"E39.5")])],"isStart":false});
            extrude(context, id + "F26", {"entities" : qUnion([Q0]), "operationType" : NewBodyOperationType.ADD, "oppositeDirection" : true, "depth" : 69.85 * mm, "offsetDistance" : 25.4 * mm, "hasSecondDirection" : true, "secondDirectionOppositeDirection" : true, "secondDirectionDepth" : 63.5 * mm});
        }
        {
            var Q0;
            Q0=makeQuery(id+"F25.opExtrude","CAP_FACE",FACE,{"disambiguationData":[OSD([sQuery(id+"F23.wireOp",EDGE,"E42"),sQuery(id+"F23.wireOp",EDGE,"E43.0"),sQuery(id+"F23.wireOp",EDGE,"E43.1"),sQuery(id+"F23.wireOp",EDGE,"E43.2"),sQuery(id+"F23.wireOp",EDGE,"E43.3"),sQuery(id+"F23.wireOp",EDGE,"E43.4"),sQuery(id+"F23.wireOp",EDGE,"E43.5")])],"isStart":false});
            extrude(context, id + "F27", {"entities" : qUnion([Q0]), "operationType" : NewBodyOperationType.ADD, "oppositeDirection" : true, "depth" : 69.85 * mm, "offsetDistance" : 25.4 * mm, "hasSecondDirection" : true, "secondDirectionOppositeDirection" : true, "secondDirectionDepth" : 63.5 * mm});
        }
    });
